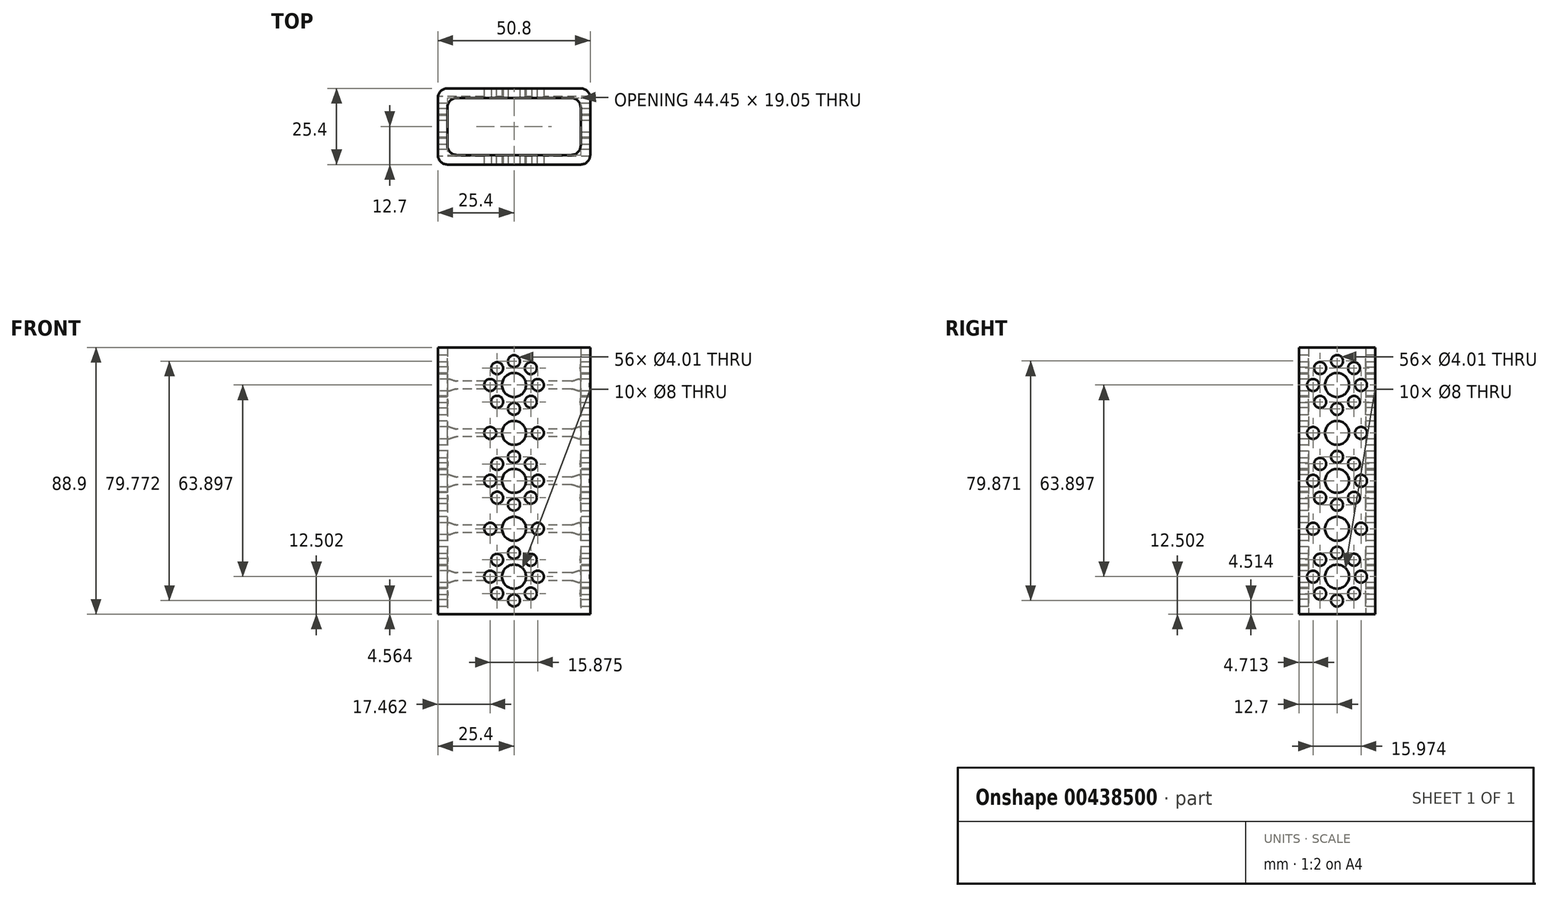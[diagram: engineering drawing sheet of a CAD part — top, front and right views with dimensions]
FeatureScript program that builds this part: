
annotation { "Feature Type Name" : "Feature", "Feature Type Description" : "" }
export const myFeature = defineFeature(function(context is Context, id is Id, definition is map)
    precondition{}
    {
        {
            var Q0;
            Q0=qCreatedBy(makeId("Top.planeOp"),FACE);
            var sketch = newSketch(context, id + "F0", { "sketchPlane" : qUnion([Q0])});
            skLineSegment(sketch, "E0.bottom", {"start": v(22.23, 12.7) * mm, "end": v(-22.22, 12.7) * mm});
            skLineSegment(sketch, "E0.top", {"start": v(22.23, -12.7) * mm, "end": v(-22.22, -12.7) * mm});
            skLineSegment(sketch, "E0.left", {"start": v(25.4, 9.53) * mm, "end": v(25.4, -9.53) * mm});
            skLineSegment(sketch, "E0.right", {"start": v(-25.4, 9.52) * mm, "end": v(-25.4, -9.53) * mm});
            skPoint(sketch, "E0.middle", {"position": v(0, 0) * mm});
            skPoint(sketch, "E1.visualSharp", {"position": v(-25.4, 12.7) * mm});
            skArc(sketch, "E1.filletArc", {"start": v(-22.22, 12.7) * mm, "mid": v(-24.47, 11.77) * mm, "end": v(-25.4, 9.52) * mm});
            skPoint(sketch, "E2.visualSharp", {"position": v(25.4, 12.7) * mm});
            skArc(sketch, "E2.filletArc", {"start": v(25.4, 9.53) * mm, "mid": v(24.47, 11.77) * mm, "end": v(22.23, 12.7) * mm});
            skPoint(sketch, "E3.visualSharp", {"position": v(25.4, -12.7) * mm});
            skArc(sketch, "E3.filletArc", {"start": v(22.23, -12.7) * mm, "mid": v(24.47, -11.77) * mm, "end": v(25.4, -9.53) * mm});
            skPoint(sketch, "E4.visualSharp", {"position": v(-25.4, -12.7) * mm});
            skArc(sketch, "E4.filletArc", {"start": v(-25.4, -9.53) * mm, "mid": v(-24.47, -11.77) * mm, "end": v(-22.22, -12.7) * mm});
            skLineSegment(sketch, "E5.bottom", {"start": v(19.05, 9.53) * mm, "end": v(-19.05, 9.53) * mm});
            skLineSegment(sketch, "E5.top", {"start": v(19.05, -9.53) * mm, "end": v(-19.05, -9.53) * mm});
            skLineSegment(sketch, "E5.left", {"start": v(22.23, 6.35) * mm, "end": v(22.23, -6.35) * mm});
            skLineSegment(sketch, "E5.right", {"start": v(-22.23, 6.35) * mm, "end": v(-22.23, -6.35) * mm});
            skPoint(sketch, "E6.visualSharp", {"position": v(22.22, 9.53) * mm});
            skArc(sketch, "E6.filletArc", {"start": v(22.23, 6.35) * mm, "mid": v(21.3, 8.6) * mm, "end": v(19.05, 9.53) * mm});
            skArc(sketch, "E7.filletArc", {"start": v(19.05, -9.53) * mm, "mid": v(21.3, -8.6) * mm, "end": v(22.23, -6.35) * mm});
            skPoint(sketch, "E8.visualSharp", {"position": v(-22.23, -9.53) * mm});
            skArc(sketch, "E8.filletArc", {"start": v(-22.23, -6.35) * mm, "mid": v(-21.3, -8.6) * mm, "end": v(-19.05, -9.53) * mm});
            skPoint(sketch, "E9.visualSharp", {"position": v(-22.23, 9.53) * mm});
            skArc(sketch, "E9.filletArc", {"start": v(-19.05, 9.53) * mm, "mid": v(-21.3, 8.6) * mm, "end": v(-22.23, 6.35) * mm});
            skSolve(sketch);
        }
        {
            var Q0;
            Q0=makeQuery(id+"F0.imprint","IMPRINT",FACE,{"disambiguationData":[TD([[makeQuery(id+"F0.imprint","IMPRINT",EDGE,{"derivedFrom":sQuery(id+"F0.wireOp",EDGE,"E0.bottom")}),1.0]])]});
            extrude(context, id + "F1", {"entities" : qUnion([Q0]), "depth" : 88.9 * mm});
        }
        {
            var Q0;
            Q0=makeQuery(id+"F1.opExtrude","SWEPT_FACE",FACE,{"disambiguationData":[OSD([sQuery(id+"F0.wireOp",EDGE,"E0.top")])]});
            var sketch = newSketch(context, id + "F2", { "sketchPlane" : qUnion([Q0])});
            skPoint(sketch, "E10", {"position": v(0, 44.45) * mm});
            skPoint(sketch, "E11", {"position": v(0, 52.39) * mm});
            skPoint(sketch, "E12.1.0", {"position": v(-5.61, 50.06) * mm});
            skPoint(sketch, "E12.2.0", {"position": v(-7.94, 44.45) * mm});
            skPoint(sketch, "E12.3.0", {"position": v(-5.61, 38.84) * mm});
            skPoint(sketch, "E12.4.0", {"position": v(0, 36.51) * mm});
            skPoint(sketch, "E12.5.0", {"position": v(5.61, 38.84) * mm});
            skPoint(sketch, "E12.6.0", {"position": v(7.94, 44.45) * mm});
            skPoint(sketch, "E12.7.0", {"position": v(5.61, 50.06) * mm});
            skPoint(sketch, "E13", {"position": v(0, 76.4) * mm});
            skPoint(sketch, "E14", {"position": v(0, 84.34) * mm});
            skPoint(sketch, "E15.1.0", {"position": v(-5.61, 82.01) * mm});
            skPoint(sketch, "E15.2.0", {"position": v(-7.94, 76.4) * mm});
            skPoint(sketch, "E15.3.0", {"position": v(-5.61, 70.79) * mm});
            skPoint(sketch, "E15.4.0", {"position": v(0, 68.46) * mm});
            skPoint(sketch, "E15.5.0", {"position": v(5.61, 70.79) * mm});
            skPoint(sketch, "E15.6.0", {"position": v(7.94, 76.4) * mm});
            skPoint(sketch, "E15.7.0", {"position": v(5.61, 82.01) * mm});
            skPoint(sketch, "E16", {"position": v(0, 12.5) * mm});
            skPoint(sketch, "E17", {"position": v(0, 20.44) * mm});
            skPoint(sketch, "E18.1.0", {"position": v(-5.61, 18.11) * mm});
            skPoint(sketch, "E18.2.0", {"position": v(-7.94, 12.5) * mm});
            skPoint(sketch, "E18.3.0", {"position": v(-5.61, 6.89) * mm});
            skPoint(sketch, "E18.4.0", {"position": v(0, 4.56) * mm});
            skPoint(sketch, "E18.5.0", {"position": v(5.61, 6.89) * mm});
            skPoint(sketch, "E18.6.0", {"position": v(7.94, 12.5) * mm});
            skPoint(sketch, "E18.7.0", {"position": v(5.61, 18.11) * mm});
            skPoint(sketch, "E19", {"position": v(0, 60.42) * mm});
            skPoint(sketch, "E20", {"position": v(0, 28.48) * mm});
            skPoint(sketch, "E21", {"position": v(7.94, 60.42) * mm});
            skPoint(sketch, "E22", {"position": v(-7.94, 60.42) * mm});
            skPoint(sketch, "E23", {"position": v(-7.94, 28.48) * mm});
            skPoint(sketch, "E24", {"position": v(7.94, 28.48) * mm});
            skSolve(sketch);
        }
        {
            var Q0;
            Q0=sQuery(id+"F2.wireOp",VERTEX,"E10");
            var Q1;
            Q1=makeQuery(id+"F1.opExtrude","SWEPT_BODY",BODY,{"disambiguationData":[OSD([sQuery(id+"F0.wireOp",EDGE,"E0.bottom"),sQuery(id+"F0.wireOp",EDGE,"E0.top"),sQuery(id+"F0.wireOp",EDGE,"E0.left"),sQuery(id+"F0.wireOp",EDGE,"E0.right"),sQuery(id+"F0.wireOp",EDGE,"E1.filletArc"),sQuery(id+"F0.wireOp",EDGE,"E2.filletArc"),sQuery(id+"F0.wireOp",EDGE,"E3.filletArc"),sQuery(id+"F0.wireOp",EDGE,"E4.filletArc"),sQuery(id+"F0.wireOp",EDGE,"E5.bottom"),sQuery(id+"F0.wireOp",EDGE,"E5.top"),sQuery(id+"F0.wireOp",EDGE,"E5.left"),sQuery(id+"F0.wireOp",EDGE,"E5.right"),sQuery(id+"F0.wireOp",EDGE,"E6.filletArc"),sQuery(id+"F0.wireOp",EDGE,"E7.filletArc"),sQuery(id+"F0.wireOp",EDGE,"E8.filletArc"),sQuery(id+"F0.wireOp",EDGE,"E9.filletArc")])]});
            hole(context, id + "F3", {"style" : HoleStyle.SIMPLE, "endStyle" : HoleEndStyle.THROUGH, "holeDiameter" : 8 * mm, "locations" : qUnion([Q0]), "scope" : qUnion([Q1]), "isTappedThrough" : true});
        }
        {
            var Q0;
            Q0=sQuery(id+"F2.wireOp",VERTEX,"E13");
            var Q1;
            Q1=sQuery(id+"F2.wireOp",VERTEX,"E16");
            var Q2;
            Q2=sQuery(id+"F2.wireOp",VERTEX,"E19");
            var Q3;
            Q3=sQuery(id+"F2.wireOp",VERTEX,"E20");
            var Q4;
            Q4=makeQuery(id+"F1.opExtrude","SWEPT_BODY",BODY,{"disambiguationData":[OSD([sQuery(id+"F0.wireOp",EDGE,"E0.bottom"),sQuery(id+"F0.wireOp",EDGE,"E0.top"),sQuery(id+"F0.wireOp",EDGE,"E0.left"),sQuery(id+"F0.wireOp",EDGE,"E0.right"),sQuery(id+"F0.wireOp",EDGE,"E1.filletArc"),sQuery(id+"F0.wireOp",EDGE,"E2.filletArc"),sQuery(id+"F0.wireOp",EDGE,"E3.filletArc"),sQuery(id+"F0.wireOp",EDGE,"E4.filletArc"),sQuery(id+"F0.wireOp",EDGE,"E5.bottom"),sQuery(id+"F0.wireOp",EDGE,"E5.top"),sQuery(id+"F0.wireOp",EDGE,"E5.left"),sQuery(id+"F0.wireOp",EDGE,"E5.right"),sQuery(id+"F0.wireOp",EDGE,"E6.filletArc"),sQuery(id+"F0.wireOp",EDGE,"E7.filletArc"),sQuery(id+"F0.wireOp",EDGE,"E8.filletArc"),sQuery(id+"F0.wireOp",EDGE,"E9.filletArc")])]});
            hole(context, id + "F4", {"style" : HoleStyle.SIMPLE, "endStyle" : HoleEndStyle.THROUGH, "holeDiameter" : 8 * mm, "locations" : qUnion([Q0, Q1, Q2, Q3]), "scope" : qUnion([Q4]), "isTappedThrough" : true});
        }
        {
            var Q0;
            Q0=sQuery(id+"F2.wireOp",VERTEX,"E15.2.0");
            var Q1;
            Q1=sQuery(id+"F2.wireOp",VERTEX,"E15.6.0");
            var Q2;
            Q2=sQuery(id+"F2.wireOp",VERTEX,"E15.5.0");
            var Q3;
            Q3=sQuery(id+"F2.wireOp",VERTEX,"E15.4.0");
            var Q4;
            Q4=sQuery(id+"F2.wireOp",VERTEX,"E15.3.0");
            var Q5;
            Q5=sQuery(id+"F2.wireOp",VERTEX,"E22");
            var Q6;
            Q6=sQuery(id+"F2.wireOp",VERTEX,"E21");
            var Q7;
            Q7=sQuery(id+"F2.wireOp",VERTEX,"E12.2.0");
            var Q8;
            Q8=sQuery(id+"F2.wireOp",VERTEX,"E12.1.0");
            var Q9;
            Q9=sQuery(id+"F2.wireOp",VERTEX,"E11");
            var Q10;
            Q10=sQuery(id+"F2.wireOp",VERTEX,"E12.7.0");
            var Q11;
            Q11=sQuery(id+"F2.wireOp",VERTEX,"E12.6.0");
            var Q12;
            Q12=sQuery(id+"F2.wireOp",VERTEX,"E12.5.0");
            var Q13;
            Q13=sQuery(id+"F2.wireOp",VERTEX,"E12.4.0");
            var Q14;
            Q14=sQuery(id+"F2.wireOp",VERTEX,"E12.3.0");
            var Q15;
            Q15=sQuery(id+"F2.wireOp",VERTEX,"E23");
            var Q16;
            Q16=sQuery(id+"F2.wireOp",VERTEX,"E24");
            var Q17;
            Q17=sQuery(id+"F2.wireOp",VERTEX,"E18.1.0");
            var Q18;
            Q18=sQuery(id+"F2.wireOp",VERTEX,"E18.7.0");
            var Q19;
            Q19=sQuery(id+"F2.wireOp",VERTEX,"E18.6.0");
            var Q20;
            Q20=sQuery(id+"F2.wireOp",VERTEX,"E17");
            var Q21;
            Q21=sQuery(id+"F2.wireOp",VERTEX,"E18.2.0");
            var Q22;
            Q22=sQuery(id+"F2.wireOp",VERTEX,"E15.1.0");
            var Q23;
            Q23=sQuery(id+"F2.wireOp",VERTEX,"E14");
            var Q24;
            Q24=sQuery(id+"F2.wireOp",VERTEX,"E15.7.0");
            var Q25;
            Q25=sQuery(id+"F2.wireOp",VERTEX,"E18.3.0");
            var Q26;
            Q26=sQuery(id+"F2.wireOp",VERTEX,"E18.4.0");
            var Q27;
            Q27=sQuery(id+"F2.wireOp",VERTEX,"E18.5.0");
            var Q28;
            Q28=makeQuery(id+"F1.opExtrude","SWEPT_BODY",BODY,{"disambiguationData":[OSD([sQuery(id+"F0.wireOp",EDGE,"E0.bottom"),sQuery(id+"F0.wireOp",EDGE,"E0.top"),sQuery(id+"F0.wireOp",EDGE,"E0.left"),sQuery(id+"F0.wireOp",EDGE,"E0.right"),sQuery(id+"F0.wireOp",EDGE,"E1.filletArc"),sQuery(id+"F0.wireOp",EDGE,"E2.filletArc"),sQuery(id+"F0.wireOp",EDGE,"E3.filletArc"),sQuery(id+"F0.wireOp",EDGE,"E4.filletArc"),sQuery(id+"F0.wireOp",EDGE,"E5.bottom"),sQuery(id+"F0.wireOp",EDGE,"E5.top"),sQuery(id+"F0.wireOp",EDGE,"E5.left"),sQuery(id+"F0.wireOp",EDGE,"E5.right"),sQuery(id+"F0.wireOp",EDGE,"E6.filletArc"),sQuery(id+"F0.wireOp",EDGE,"E7.filletArc"),sQuery(id+"F0.wireOp",EDGE,"E8.filletArc"),sQuery(id+"F0.wireOp",EDGE,"E9.filletArc")])]});
            hole(context, id + "F5", {"style" : HoleStyle.SIMPLE, "endStyle" : HoleEndStyle.THROUGH, "holeDiameter" : 4 * mm, "locations" : qUnion([Q0, Q1, Q2, Q3, Q4, Q5, Q6, Q7, Q8, Q9, Q10, Q11, Q12, Q13, Q14, Q15, Q16, Q17, Q18, Q19, Q20, Q21, Q22, Q23, Q24, Q25, Q26, Q27]), "scope" : qUnion([Q28]), "isTappedThrough" : true});
        }
        {
            var Q0;
            Q0=makeQuery(id+"F1.opExtrude","SWEPT_FACE",FACE,{"disambiguationData":[OSD([sQuery(id+"F0.wireOp",EDGE,"E0.right")])]});
            var sketch = newSketch(context, id + "F6", { "sketchPlane" : qUnion([Q0])});
            skPoint(sketch, "E25", {"position": v(0, 44.45) * mm});
            skPoint(sketch, "E26", {"position": v(0, 76.4) * mm});
            skPoint(sketch, "E27", {"position": v(0, 12.5) * mm});
            skPoint(sketch, "E28", {"position": v(0, 60.42) * mm});
            skPoint(sketch, "E29", {"position": v(0, 28.48) * mm});
            skPoint(sketch, "E30", {"position": v(-7.99, 76.4) * mm});
            skPoint(sketch, "E31.1.0", {"position": v(-5.65, 70.75) * mm});
            skPoint(sketch, "E31.2.0", {"position": v(0, 68.41) * mm});
            skPoint(sketch, "E31.3.0", {"position": v(5.65, 70.75) * mm});
            skPoint(sketch, "E31.4.0", {"position": v(7.99, 76.4) * mm});
            skPoint(sketch, "E31.5.0", {"position": v(5.65, 82.05) * mm});
            skPoint(sketch, "E31.6.0", {"position": v(0, 84.39) * mm});
            skPoint(sketch, "E31.7.0", {"position": v(-5.65, 82.05) * mm});
            skPoint(sketch, "E32", {"position": v(-7.99, 44.45) * mm});
            skPoint(sketch, "E33", {"position": v(-7.99, 60.42) * mm});
            skPoint(sketch, "E34", {"position": v(7.99, 60.42) * mm});
            skPoint(sketch, "E35", {"position": v(-7.99, 28.48) * mm});
            skPoint(sketch, "E36", {"position": v(7.99, 28.48) * mm});
            skPoint(sketch, "E37", {"position": v(7.99, 44.45) * mm});
            skPoint(sketch, "E38", {"position": v(7.99, 12.5) * mm});
            skPoint(sketch, "E39", {"position": v(-7.99, 12.5) * mm});
            skPoint(sketch, "E40.1.0", {"position": v(-5.65, 6.85) * mm});
            skPoint(sketch, "E40.2.0", {"position": v(0, 4.51) * mm});
            skPoint(sketch, "E40.3.0", {"position": v(5.65, 6.85) * mm});
            skPoint(sketch, "E40.5.0", {"position": v(5.65, 18.15) * mm});
            skPoint(sketch, "E40.6.0", {"position": v(0, 20.49) * mm});
            skPoint(sketch, "E40.7.0", {"position": v(-5.65, 18.15) * mm});
            skPoint(sketch, "E41.1.0", {"position": v(-5.65, 38.8) * mm});
            skPoint(sketch, "E41.2.0", {"position": v(0, 36.46) * mm});
            skPoint(sketch, "E41.3.0", {"position": v(5.65, 38.8) * mm});
            skPoint(sketch, "E41.5.0", {"position": v(5.65, 50.1) * mm});
            skPoint(sketch, "E41.6.0", {"position": v(0, 52.44) * mm});
            skPoint(sketch, "E41.7.0", {"position": v(-5.65, 50.1) * mm});
            skSolve(sketch);
        }
        {
            var Q0;
            Q0=sQuery(id+"F6.wireOp",VERTEX,"E26");
            var Q1;
            Q1=sQuery(id+"F6.wireOp",VERTEX,"E28");
            var Q2;
            Q2=sQuery(id+"F6.wireOp",VERTEX,"E25");
            var Q3;
            Q3=sQuery(id+"F6.wireOp",VERTEX,"E29");
            var Q4;
            Q4=sQuery(id+"F6.wireOp",VERTEX,"E27");
            var Q5;
            Q5=makeQuery(id+"F1.opExtrude","SWEPT_BODY",BODY,{"disambiguationData":[OSD([sQuery(id+"F0.wireOp",EDGE,"E0.bottom"),sQuery(id+"F0.wireOp",EDGE,"E0.top"),sQuery(id+"F0.wireOp",EDGE,"E0.left"),sQuery(id+"F0.wireOp",EDGE,"E0.right"),sQuery(id+"F0.wireOp",EDGE,"E1.filletArc"),sQuery(id+"F0.wireOp",EDGE,"E2.filletArc"),sQuery(id+"F0.wireOp",EDGE,"E3.filletArc"),sQuery(id+"F0.wireOp",EDGE,"E4.filletArc"),sQuery(id+"F0.wireOp",EDGE,"E5.bottom"),sQuery(id+"F0.wireOp",EDGE,"E5.top"),sQuery(id+"F0.wireOp",EDGE,"E5.left"),sQuery(id+"F0.wireOp",EDGE,"E5.right"),sQuery(id+"F0.wireOp",EDGE,"E6.filletArc"),sQuery(id+"F0.wireOp",EDGE,"E7.filletArc"),sQuery(id+"F0.wireOp",EDGE,"E8.filletArc"),sQuery(id+"F0.wireOp",EDGE,"E9.filletArc")])]});
            hole(context, id + "F7", {"style" : HoleStyle.SIMPLE, "endStyle" : HoleEndStyle.THROUGH, "holeDiameter" : 8 * mm, "locations" : qUnion([Q0, Q1, Q2, Q3, Q4]), "scope" : qUnion([Q5]), "isTappedThrough" : true});
        }
        {
            var Q0;
            Q0=sQuery(id+"F6.wireOp",VERTEX,"E33");
            var Q1;
            Q1=sQuery(id+"F6.wireOp",VERTEX,"E29");
            var Q2;
            Q2=sQuery(id+"F6.wireOp",VERTEX,"E36");
            var Q3;
            Q3=sQuery(id+"F6.wireOp",VERTEX,"E39");
            var Q4;
            Q4=sQuery(id+"F6.wireOp",VERTEX,"E27");
            var Q5;
            Q5=sQuery(id+"F6.wireOp",VERTEX,"E34");
            var Q6;
            Q6=sQuery(id+"F6.wireOp",VERTEX,"E31.1.0");
            var Q7;
            Q7=sQuery(id+"F6.wireOp",VERTEX,"E41.1.0");
            var Q8;
            Q8=sQuery(id+"F6.wireOp",VERTEX,"E41.5.0");
            var Q9;
            Q9=sQuery(id+"F6.wireOp",VERTEX,"E31.3.0");
            var Q10;
            Q10=sQuery(id+"F6.wireOp",VERTEX,"E40.6.0");
            var Q11;
            Q11=sQuery(id+"F6.wireOp",VERTEX,"E25");
            var Q12;
            Q12=sQuery(id+"F6.wireOp",VERTEX,"E31.2.0");
            var Q13;
            Q13=sQuery(id+"F6.wireOp",VERTEX,"E41.3.0");
            var Q14;
            Q14=sQuery(id+"F6.wireOp",VERTEX,"E38");
            var Q15;
            Q15=sQuery(id+"F6.wireOp",VERTEX,"E31.4.0");
            var Q16;
            Q16=sQuery(id+"F6.wireOp",VERTEX,"E30");
            var Q17;
            Q17=sQuery(id+"F6.wireOp",VERTEX,"E37");
            var Q18;
            Q18=sQuery(id+"F6.wireOp",VERTEX,"E35");
            var Q19;
            Q19=sQuery(id+"F6.wireOp",VERTEX,"E41.6.0");
            var Q20;
            Q20=sQuery(id+"F6.wireOp",VERTEX,"E32");
            var Q21;
            Q21=sQuery(id+"F6.wireOp",VERTEX,"E40.5.0");
            var Q22;
            Q22=sQuery(id+"F6.wireOp",VERTEX,"E41.2.0");
            var Q23;
            Q23=sQuery(id+"F6.wireOp",VERTEX,"E40.7.0");
            var Q24;
            Q24=sQuery(id+"F6.wireOp",VERTEX,"E28");
            var Q25;
            Q25=sQuery(id+"F6.wireOp",VERTEX,"E41.7.0");
            var Q26;
            Q26=sQuery(id+"F6.wireOp",VERTEX,"E26");
            var Q27;
            Q27=sQuery(id+"F6.wireOp",VERTEX,"E31.7.0");
            var Q28;
            Q28=sQuery(id+"F6.wireOp",VERTEX,"E31.6.0");
            var Q29;
            Q29=sQuery(id+"F6.wireOp",VERTEX,"E31.5.0");
            var Q30;
            Q30=sQuery(id+"F6.wireOp",VERTEX,"E40.1.0");
            var Q31;
            Q31=sQuery(id+"F6.wireOp",VERTEX,"E40.2.0");
            var Q32;
            Q32=sQuery(id+"F6.wireOp",VERTEX,"E40.3.0");
            var Q33;
            Q33=makeQuery(id+"F1.opExtrude","SWEPT_BODY",BODY,{"disambiguationData":[OSD([sQuery(id+"F0.wireOp",EDGE,"E0.bottom"),sQuery(id+"F0.wireOp",EDGE,"E0.top"),sQuery(id+"F0.wireOp",EDGE,"E0.left"),sQuery(id+"F0.wireOp",EDGE,"E0.right"),sQuery(id+"F0.wireOp",EDGE,"E1.filletArc"),sQuery(id+"F0.wireOp",EDGE,"E2.filletArc"),sQuery(id+"F0.wireOp",EDGE,"E3.filletArc"),sQuery(id+"F0.wireOp",EDGE,"E4.filletArc"),sQuery(id+"F0.wireOp",EDGE,"E5.bottom"),sQuery(id+"F0.wireOp",EDGE,"E5.top"),sQuery(id+"F0.wireOp",EDGE,"E5.left"),sQuery(id+"F0.wireOp",EDGE,"E5.right"),sQuery(id+"F0.wireOp",EDGE,"E6.filletArc"),sQuery(id+"F0.wireOp",EDGE,"E7.filletArc"),sQuery(id+"F0.wireOp",EDGE,"E8.filletArc"),sQuery(id+"F0.wireOp",EDGE,"E9.filletArc")])]});
            hole(context, id + "F8", {"style" : HoleStyle.SIMPLE, "endStyle" : HoleEndStyle.THROUGH, "holeDiameter" : 4 * mm, "locations" : qUnion([Q0, Q1, Q2, Q3, Q4, Q5, Q6, Q7, Q8, Q9, Q10, Q11, Q12, Q13, Q14, Q15, Q16, Q17, Q18, Q19, Q20, Q21, Q22, Q23, Q24, Q25, Q26, Q27, Q28, Q29, Q30, Q31, Q32]), "scope" : qUnion([Q33]), "isTappedThrough" : true});
        }
    });
